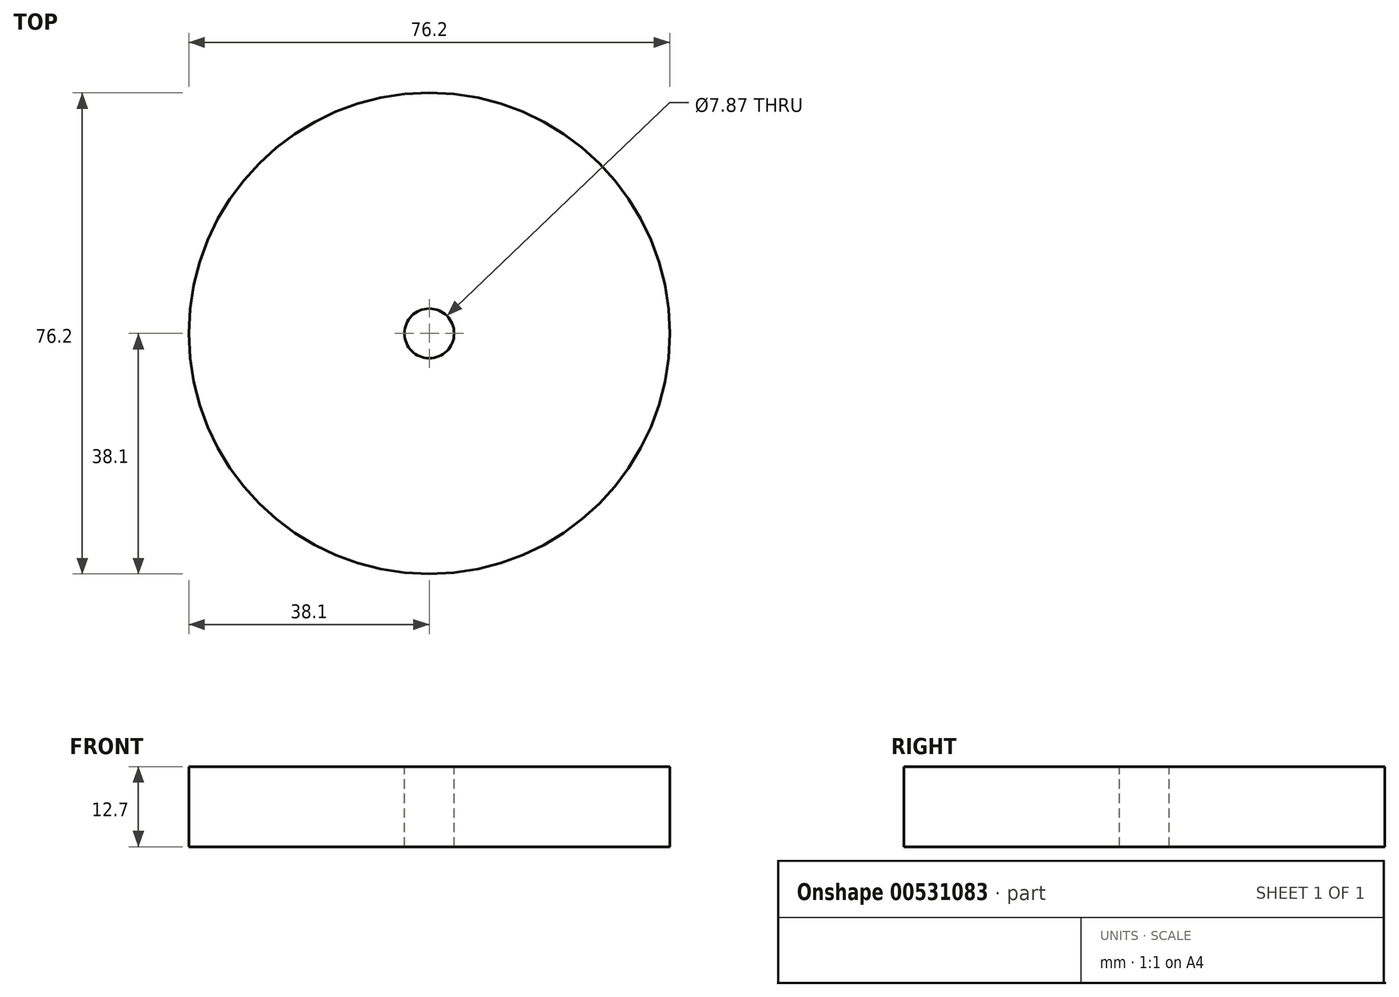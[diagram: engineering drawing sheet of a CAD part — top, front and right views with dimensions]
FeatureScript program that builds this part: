
annotation { "Feature Type Name" : "Feature", "Feature Type Description" : "" }
export const myFeature = defineFeature(function(context is Context, id is Id, definition is map)
    precondition{}
    {
        {
            var Q0;
            Q0=qCreatedBy(makeId("Top.planeOp"),FACE);
            var sketch = newSketch(context, id + "F0", { "sketchPlane" : qUnion([Q0])});
            skCircle(sketch, "E0", {"center": v(0, 0) * mm, "radius": 38.1 * mm});
            skSolve(sketch);
        }
        {
            var Q0;
            Q0=makeQuery(id+"F0.imprint","IMPRINT",FACE,{"disambiguationData":[TD([[makeQuery(id+"F0.imprint","IMPRINT",EDGE,{"derivedFrom":sQuery(id+"F0.wireOp",EDGE,"E0")}),1.0]])]});
            extrude(context, id + "F1", {"entities" : qUnion([Q0]), "oppositeDirection" : true, "depth" : 12.7 * mm, "offsetDistance" : 25.4 * mm});
        }
        {
            var Q0;
            Q0=makeQuery(id+"F1.opExtrude","CAP_FACE",FACE,{"disambiguationData":[OSD([sQuery(id+"F0.wireOp",EDGE,"E0")])],"isStart":true});
            var sketch = newSketch(context, id + "F2", { "sketchPlane" : qUnion([Q0])});
            skCircle(sketch, "E1", {"center": v(0, 0) * mm, "radius": 3.94 * mm});
            skSolve(sketch);
        }
        {
            var Q0;
            Q0=sQuery(id+"F2.wireOp",VERTEX,"E1.center");
            var Q1;
            Q1=makeQuery(id+"F1.opExtrude","SWEPT_BODY",BODY,{"disambiguationData":[OSD([sQuery(id+"F0.wireOp",EDGE,"E0")])]});
            hole(context, id + "F3", {"style" : HoleStyle.SIMPLE, "endStyle" : HoleEndStyle.THROUGH, "holeDiameter" : 7.87 * mm, "isTappedThrough" : true, "tappedDepth" : 12.7 * mm, "tapClearance" : 3, "locations" : qUnion([Q0]), "scope" : qUnion([Q1])});
        }
    });
